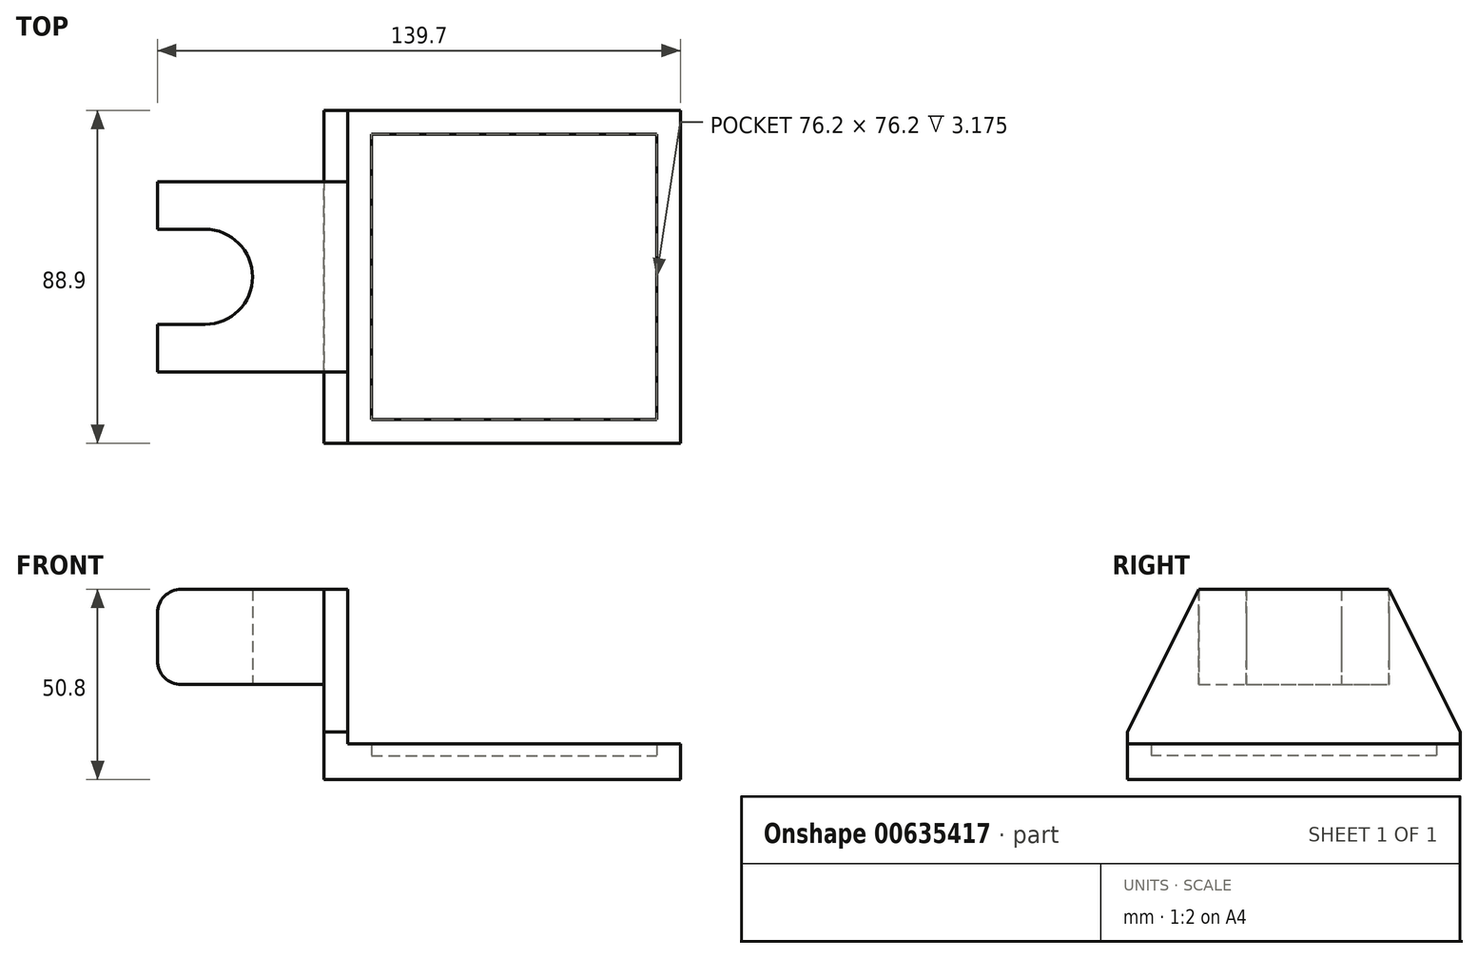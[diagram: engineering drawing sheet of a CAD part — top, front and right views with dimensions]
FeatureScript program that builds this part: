
annotation { "Feature Type Name" : "Feature", "Feature Type Description" : "" }
export const myFeature = defineFeature(function(context is Context, id is Id, definition is map)
    precondition{}
    {
        {
            var Q0;
            Q0=qCreatedBy(makeId("Top.planeOp"),FACE);
            var sketch = newSketch(context, id + "F0", { "sketchPlane" : qUnion([Q0])});
            skArc(sketch, "E0", {"start": v(0, -12.7) * mm, "mid": v(12.7, 0) * mm, "end": v(0, 12.7) * mm});
            skLineSegment(sketch, "E1", {"start": v(0, 12.7) * mm, "end": v(-12.7, 12.7) * mm});
            skLineSegment(sketch, "E2", {"start": v(-12.7, 12.7) * mm, "end": v(-12.7, 25.4) * mm});
            skLineSegment(sketch, "E3", {"start": v(-12.7, 25.4) * mm, "end": v(38.1, 25.4) * mm});
            skLineSegment(sketch, "E4", {"start": v(38.1, 25.4) * mm, "end": v(38.1, -25.4) * mm});
            skLineSegment(sketch, "E5", {"start": v(38.1, -25.4) * mm, "end": v(-12.7, -25.4) * mm});
            skLineSegment(sketch, "E6", {"start": v(-12.7, -25.4) * mm, "end": v(-12.7, -12.7) * mm});
            skLineSegment(sketch, "E7", {"start": v(-12.7, -12.7) * mm, "end": v(0, -12.7) * mm});
            skSolve(sketch);
        }
        {
            var Q0;
            Q0 = qSketchRegion(id + "F0", true);
            extrude(context, id + "F1", {"entities" : qUnion([Q0]), "depth" : 25.4 * mm, "offsetDistance" : 25.4 * mm});
        }
        {
            var Q0;
            Q0=makeQuery(id+"F1.opExtrude","CAP_EDGE",EDGE,{"disambiguationData":[OSD([sQuery(id+"F0.wireOp",EDGE,"E6")])],"isStart":false});
            var Q1;
            Q1=makeQuery(id+"F1.opExtrude","CAP_EDGE",EDGE,{"disambiguationData":[OSD([sQuery(id+"F0.wireOp",EDGE,"E2")])],"isStart":false});
            var Q2;
            Q2=makeQuery(id+"F1.opExtrude","CAP_EDGE",EDGE,{"disambiguationData":[OSD([sQuery(id+"F0.wireOp",EDGE,"E6")])],"isStart":true});
            var Q3;
            Q3=makeQuery(id+"F1.opExtrude","CAP_EDGE",EDGE,{"disambiguationData":[OSD([sQuery(id+"F0.wireOp",EDGE,"E2")])],"isStart":true});
            fillet(context, id + "F2", {"entities" : qUnion([Q0, Q1, Q2, Q3]), "radius" : 6.35 * mm, "tangentPropagation" : true, "allowEdgeOverflow" : false});
        }
        {
            var Q0;
            Q0=qCreatedBy(makeId("Top.planeOp"),FACE);
            cPlane(context, id + "F3", {"entities" : qUnion([Q0]), "cplaneType" : CPlaneType.OFFSET, "offset" : 25.4 * mm, "oppositeDirection" : true, "width" : 152.4 * mm, "height" : 152.4 * mm});
        }
        {
            var Q0;
            Q0=qCreatedBy(id+"F3.planeOp",FACE);
            var sketch = newSketch(context, id + "F4", { "sketchPlane" : qUnion([Q0])});
            skLineSegment(sketch, "E8.bottom", {"start": v(38.1, 44.45) * mm, "end": v(127, 44.45) * mm, "construction": true});
            skLineSegment(sketch, "E8.top", {"start": v(38.1, -44.45) * mm, "end": v(127, -44.45) * mm, "construction": true});
            skLineSegment(sketch, "E8.left", {"start": v(38.1, 44.45) * mm, "end": v(38.1, -44.45) * mm, "construction": true});
            skLineSegment(sketch, "E8.right", {"start": v(127, 44.45) * mm, "end": v(127, -44.45) * mm, "construction": true});
            skLineSegment(sketch, "E9", {"start": v(38.1, 44.45) * mm, "end": v(31.75, 44.45) * mm});
            skLineSegment(sketch, "E10", {"start": v(31.75, 44.45) * mm, "end": v(31.75, -44.45) * mm});
            skLineSegment(sketch, "E11", {"start": v(31.75, -44.45) * mm, "end": v(38.1, -44.45) * mm});
            skLineSegment(sketch, "E12", {"start": v(38.1, 44.45) * mm, "end": v(38.1, -44.45) * mm});
            skSolve(sketch);
        }
        {
            var Q0;
            Q0 = qSketchRegion(id + "F4", true);
            extrude(context, id + "F5", {"entities" : qUnion([Q0]), "depth" : 12.7 * mm, "offsetDistance" : 25.4 * mm});
        }
        {
            var Q0;
            Q0=makeQuery(id+"F1.opExtrude","CAP_FACE",FACE,{"disambiguationData":[OSD([sQuery(id+"F0.wireOp",EDGE,"E0"),sQuery(id+"F0.wireOp",EDGE,"E1"),sQuery(id+"F0.wireOp",EDGE,"E2"),sQuery(id+"F0.wireOp",EDGE,"E3"),sQuery(id+"F0.wireOp",EDGE,"E4"),sQuery(id+"F0.wireOp",EDGE,"E5"),sQuery(id+"F0.wireOp",EDGE,"E6"),sQuery(id+"F0.wireOp",EDGE,"E7")])],"isStart":false});
            var sketch = newSketch(context, id + "F6", { "sketchPlane" : qUnion([Q0])});
            skLineSegment(sketch, "E13.bottom", {"start": v(38.1, 25.4) * mm, "end": v(31.75, 25.4) * mm});
            skLineSegment(sketch, "E13.top", {"start": v(38.1, -25.4) * mm, "end": v(31.75, -25.4) * mm});
            skLineSegment(sketch, "E13.left", {"start": v(38.1, 25.4) * mm, "end": v(38.1, -25.4) * mm});
            skLineSegment(sketch, "E13.right", {"start": v(31.75, 25.4) * mm, "end": v(31.75, -25.4) * mm});
            skSolve(sketch);
        }
        {
            var Q0;
            Q0=makeQuery(id+"F6.imprint","IMPRINT",FACE,{"disambiguationData":[TD([[makeQuery(id+"F6.imprint","IMPRINT",EDGE,{"derivedFrom":sQuery(id+"F6.wireOp",EDGE,"E13.bottom")}),-1.0]])]});
            var Q1;
            Q1=makeQuery(id+"F5.opExtrude","CAP_FACE",FACE,{"disambiguationData":[OSD([sQuery(id+"F4.wireOp",EDGE,"E9"),sQuery(id+"F4.wireOp",EDGE,"E10"),sQuery(id+"F4.wireOp",EDGE,"E11"),sQuery(id+"F4.wireOp",EDGE,"E12")])],"isStart":false});
            loft(context, id + "F7", {"operationType" : NewBodyOperationType.ADD, "sheetProfilesArray" : [{ "sheetProfileEntities" : qUnion([Q0]) }, { "sheetProfileEntities" : qUnion([Q1]) }]});
        }
        {
            var Q0;
            Q0=makeQuery(id+"F5.opExtrude","CAP_FACE",FACE,{"disambiguationData":[OSD([sQuery(id+"F4.wireOp",EDGE,"E9"),sQuery(id+"F4.wireOp",EDGE,"E10"),sQuery(id+"F4.wireOp",EDGE,"E11"),sQuery(id+"F4.wireOp",EDGE,"E12")])],"isStart":true});
            var sketch = newSketch(context, id + "F8", { "sketchPlane" : qUnion([Q0])});
            skLineSegment(sketch, "E14.0", {"start": v(38.1, -44.45) * mm, "end": v(127, -44.45) * mm});
            skLineSegment(sketch, "E14.1", {"start": v(38.1, 44.45) * mm, "end": v(127, 44.45) * mm});
            skLineSegment(sketch, "E14.2", {"start": v(38.1, -44.45) * mm, "end": v(38.1, 44.45) * mm});
            skLineSegment(sketch, "E14.3", {"start": v(127, -44.45) * mm, "end": v(127, 44.45) * mm});
            skLineSegment(sketch, "E14.7", {"start": v(38.1, -44.45) * mm, "end": v(38.1, 44.45) * mm});
            skSolve(sketch);
        }
        {
            var Q0;
            Q0 = qSketchRegion(id + "F8", true);
            extrude(context, id + "F9", {"entities" : qUnion([Q0]), "operationType" : NewBodyOperationType.ADD, "oppositeDirection" : true, "depth" : 6.35 * mm, "offsetDistance" : 25.4 * mm});
        }
        {
            var Q0;
            Q0=makeQuery(id+"F9.opExtrude","CAP_FACE",FACE,{"disambiguationData":[OSD([sQuery(id+"F8.wireOp",EDGE,"E14.0"),sQuery(id+"F8.wireOp",EDGE,"E14.1"),sQuery(id+"F8.wireOp",EDGE,"E14.3"),sQuery(id+"F8.wireOp",EDGE,"E14.7")])],"isStart":false});
            var sketch = newSketch(context, id + "F10", { "sketchPlane" : qUnion([Q0])});
            skLineSegment(sketch, "E15.0", {"start": v(44.45, -38.1) * mm, "end": v(120.65, -38.1) * mm});
            skLineSegment(sketch, "E15.1", {"start": v(44.45, 38.1) * mm, "end": v(44.45, -38.1) * mm});
            skLineSegment(sketch, "E15.2", {"start": v(120.65, 38.1) * mm, "end": v(44.45, 38.1) * mm});
            skLineSegment(sketch, "E15.3", {"start": v(120.65, -38.1) * mm, "end": v(120.65, 38.1) * mm});
            skLineSegment(sketch, "E16.0.0", {"start": v(38.1, -44.45) * mm, "end": v(127, -44.45) * mm});
            skLineSegment(sketch, "E16.0.1", {"start": v(127, -44.45) * mm, "end": v(127, 44.45) * mm});
            skLineSegment(sketch, "E16.0.2", {"start": v(127, 44.45) * mm, "end": v(38.1, 44.45) * mm});
            skLineSegment(sketch, "E16.0.3", {"start": v(38.1, 44.45) * mm, "end": v(38.1, -44.45) * mm});
            skSolve(sketch);
        }
        {
            var Q0;
            Q0 = qSketchRegion(id + "F10", true);
            extrude(context, id + "F11", {"entities" : qUnion([Q0]), "operationType" : NewBodyOperationType.ADD, "depth" : 3.17 * mm, "offsetDistance" : 25.4 * mm});
        }
    });
